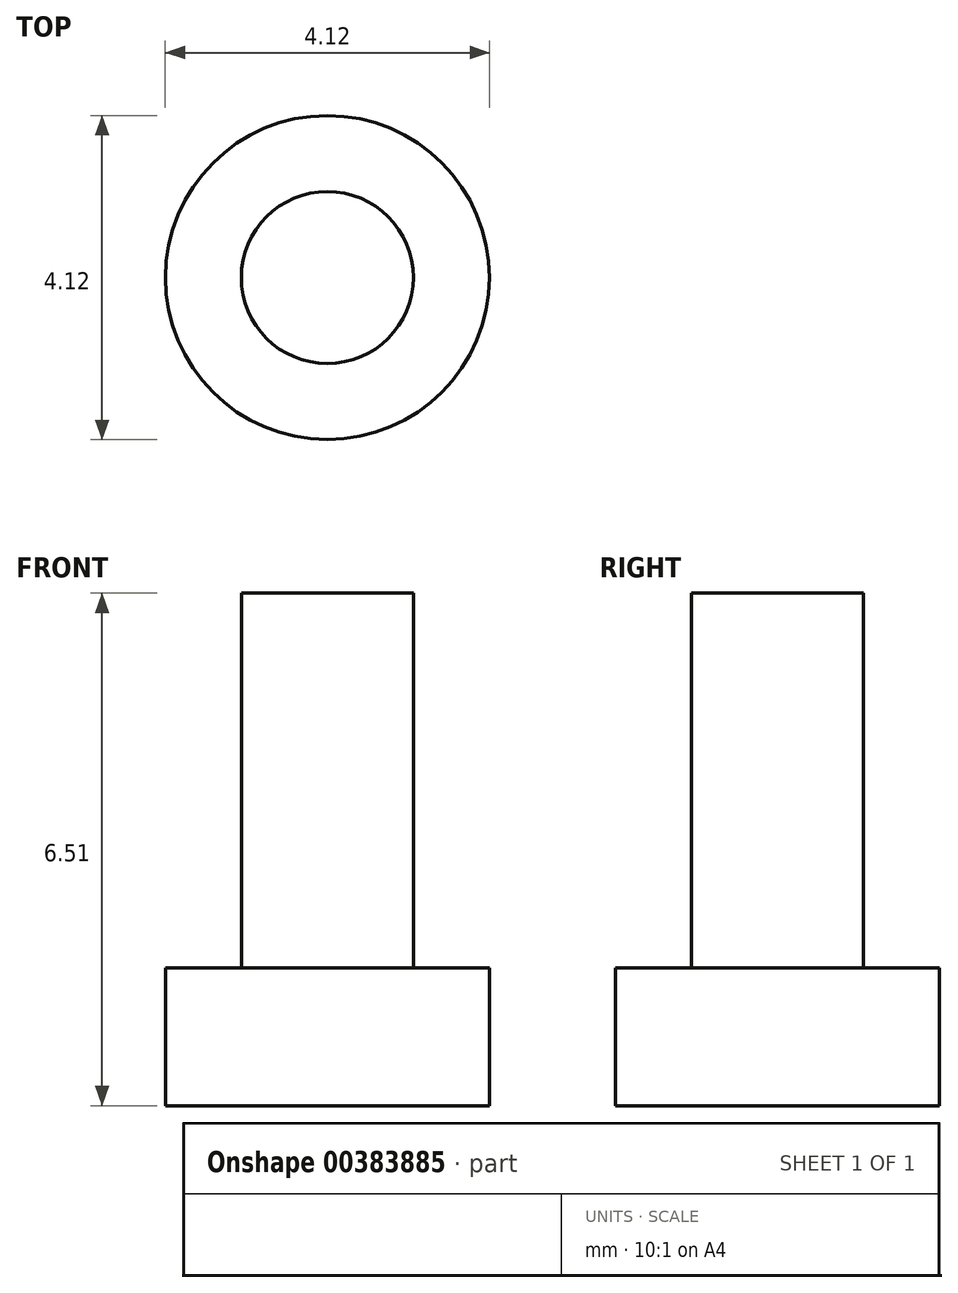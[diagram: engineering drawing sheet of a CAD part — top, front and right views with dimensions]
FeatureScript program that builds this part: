
annotation { "Feature Type Name" : "Feature", "Feature Type Description" : "" }
export const myFeature = defineFeature(function(context is Context, id is Id, definition is map)
    precondition{}
    {
        {
            var Q0;
            Q0=qCreatedBy(makeId("Top.planeOp"),FACE);
            var sketch = newSketch(context, id + "F0", { "sketchPlane" : qUnion([Q0])});
            skCircle(sketch, "E0", {"center": v(0, 0) * mm, "radius": 2.06 * mm});
            skCircle(sketch, "E1", {"center": v(0, 0) * mm, "radius": 1.1 * mm});
            skSolve(sketch);
        }
        {
            var Q0;
            Q0=makeQuery(id+"F0.imprint","IMPRINT",FACE,{"disambiguationData":[TD([[makeQuery(id+"F0.imprint","IMPRINT",EDGE,{"derivedFrom":sQuery(id+"F0.wireOp",EDGE,"E1")}),1.0]])]});
            var Q1;
            Q1=sQuery(id+"F0.wireOp",EDGE,"E1");
            extrude(context, id + "F1", {"entities" : qUnion([Q0]), "surfaceEntities" : qUnion([Q1]), "depth" : 4.76 * mm});
        }
        {
            var Q0;
            Q0 = qSketchRegion(id + "F0", true);
            var Q1;
            Q1=makeQuery(id+"F1.opExtrude","CAP_FACE",FACE,{"disambiguationData":[OSD([sQuery(id+"F0.wireOp",EDGE,"E1")])],"isStart":true});
            extrude(context, id + "F2", {"entities" : qUnion([Q0, Q1]), "operationType" : NewBodyOperationType.ADD, "depth" : -1.75 * mm});
        }
    });
